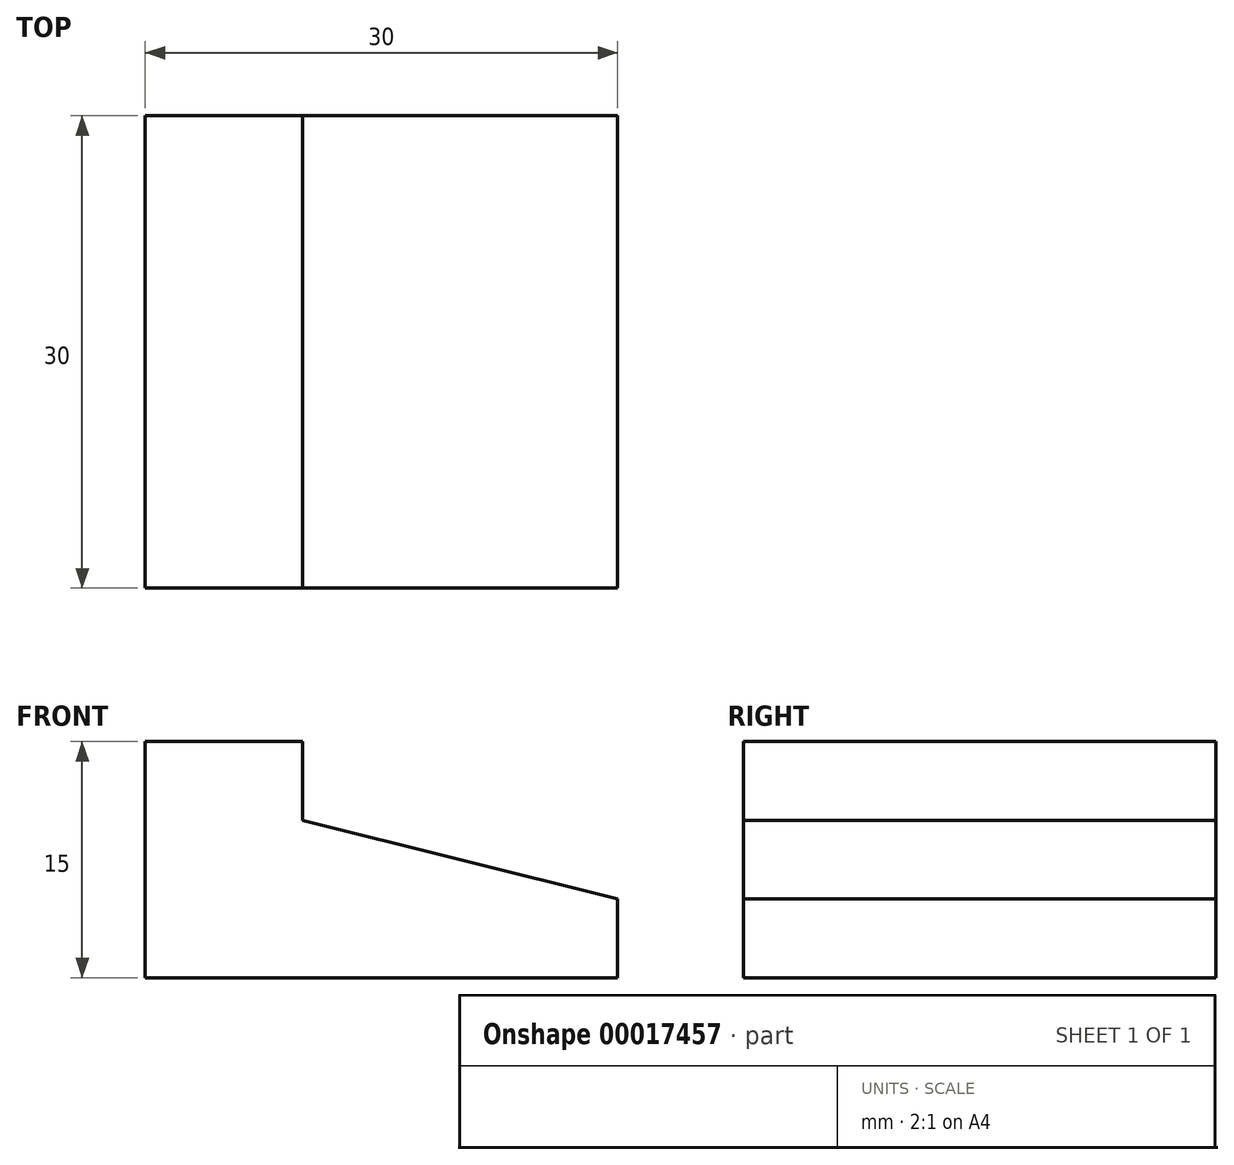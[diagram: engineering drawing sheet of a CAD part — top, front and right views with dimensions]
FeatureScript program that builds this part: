
annotation { "Feature Type Name" : "Feature", "Feature Type Description" : "" }
export const myFeature = defineFeature(function(context is Context, id is Id, definition is map)
    precondition{}
    {
        {
            var Q0;
            Q0=qCreatedBy(makeId("Front.planeOp"),FACE);
            var sketch = newSketch(context, id + "F0", { "sketchPlane" : qUnion([Q0])});
            skLineSegment(sketch, "E0", {"start": v(-48.2, 0) * mm, "end": v(-18.2, 0) * mm});
            skLineSegment(sketch, "E1", {"start": v(-48.2, 0) * mm, "end": v(-48.2, 15) * mm});
            skLineSegment(sketch, "E2", {"start": v(-48.2, 15) * mm, "end": v(-38.2, 15) * mm});
            skLineSegment(sketch, "E3", {"start": v(-38.2, 15) * mm, "end": v(-38.2, 10) * mm});
            skLineSegment(sketch, "E4", {"start": v(-38.2, 10) * mm, "end": v(-18.2, 5) * mm});
            skLineSegment(sketch, "E5", {"start": v(-18.2, 5) * mm, "end": v(-18.2, 0) * mm});
            skSolve(sketch);
        }
        {
            var Q0;
            Q0 = qSketchRegion(id + "F0", true);
            extrude(context, id + "F1", {"entities" : qUnion([Q0]), "depth" : 15 * mm});
        }
        {
            var Q0;
            Q0 = qSketchRegion(id + "F0", true);
            extrude(context, id + "F2", {"entities" : qUnion([Q0]), "operationType" : NewBodyOperationType.ADD, "depth" : 30 * mm});
        }
    });
